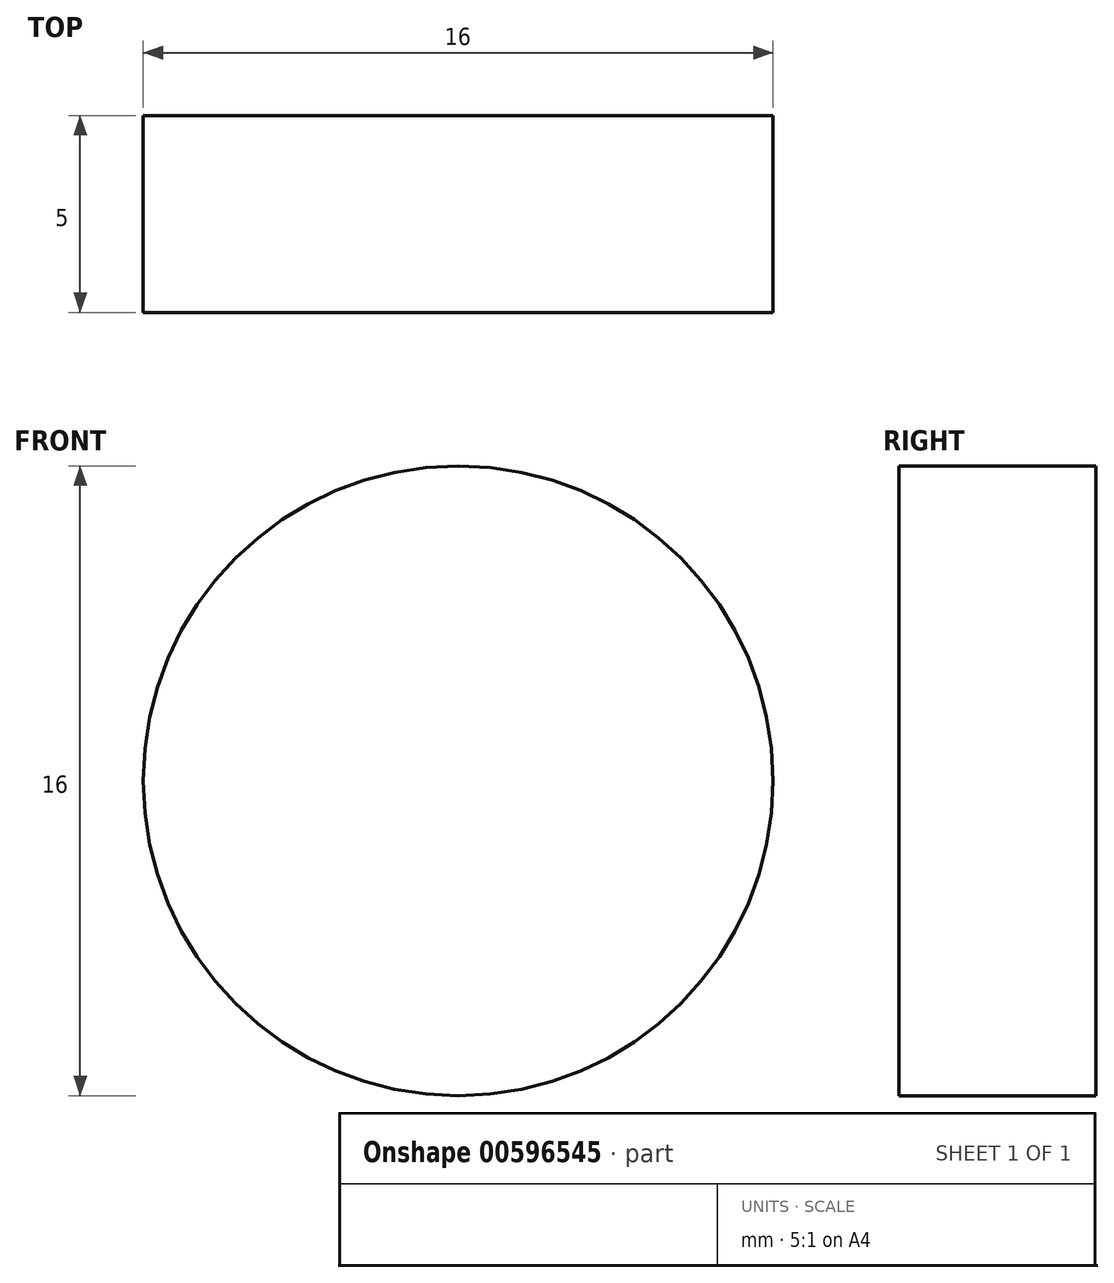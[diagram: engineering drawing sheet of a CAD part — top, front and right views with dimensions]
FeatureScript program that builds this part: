
annotation { "Feature Type Name" : "Feature", "Feature Type Description" : "" }
export const myFeature = defineFeature(function(context is Context, id is Id, definition is map)
    precondition{}
    {
        {
            var Q0;
            Q0=qCreatedBy(makeId("Front.planeOp"),FACE);
            var sketch = newSketch(context, id + "F0", { "sketchPlane" : qUnion([Q0])});
            skCircle(sketch, "E0", {"center": v(0, 0) * mm, "radius": 8 * mm});
            skSolve(sketch);
        }
        {
            var Q0;
            Q0 = qSketchRegion(id + "F0", true);
            extrude(context, id + "F1", {"entities" : qUnion([Q0]), "depth" : 5 * mm, "offsetDistance" : 25 * mm});
        }
    });
